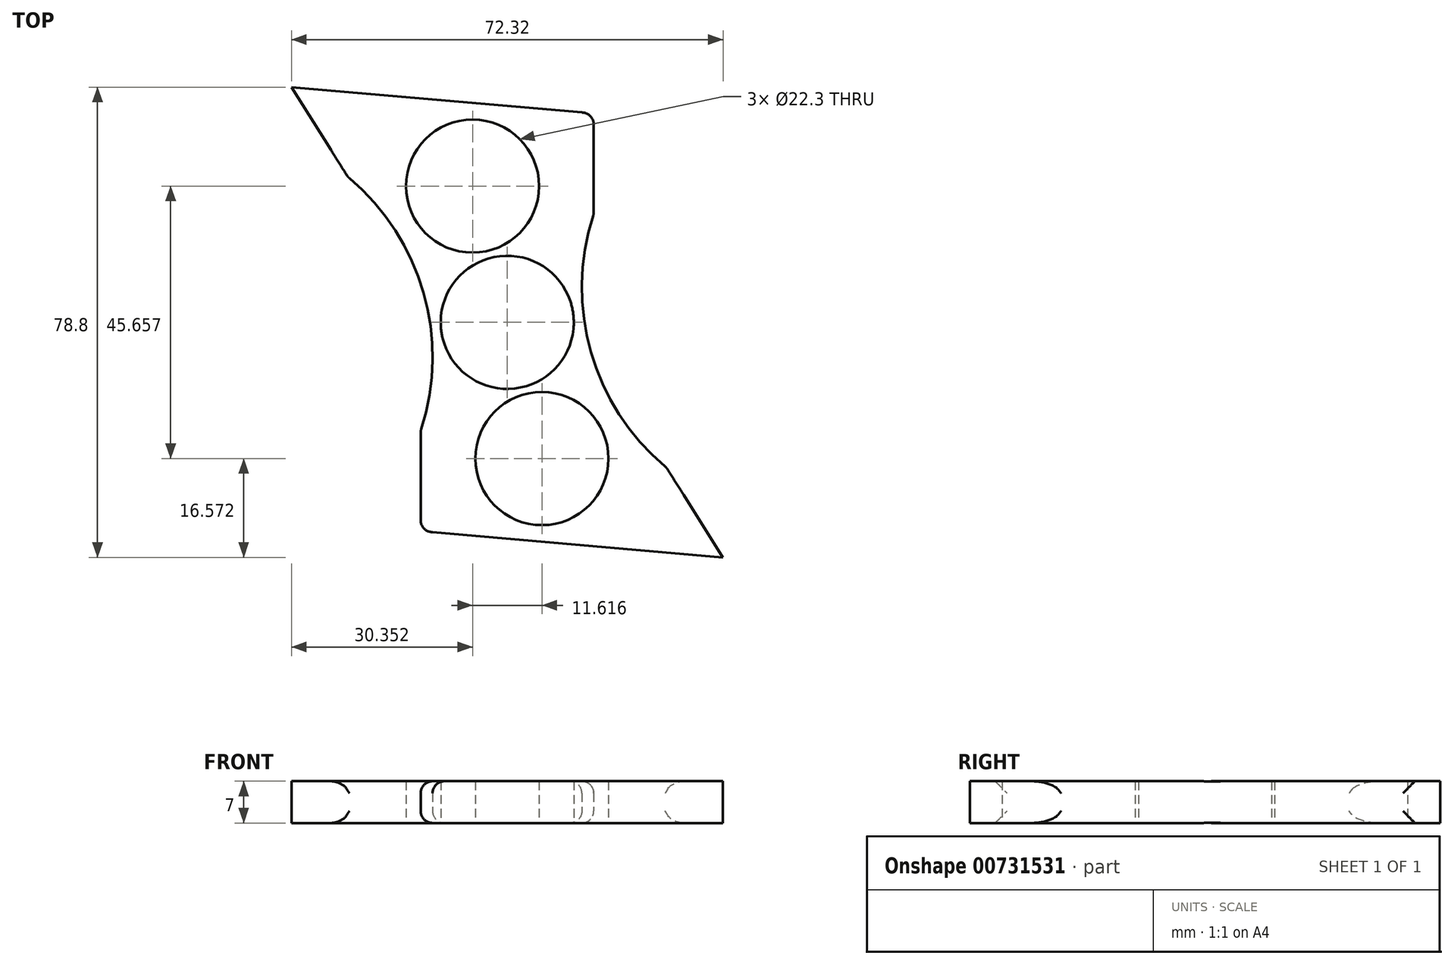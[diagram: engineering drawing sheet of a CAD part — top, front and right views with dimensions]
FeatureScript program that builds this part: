
annotation { "Feature Type Name" : "Feature", "Feature Type Description" : "" }
export const myFeature = defineFeature(function(context is Context, id is Id, definition is map)
    precondition{}
    {
        {
            var Q0;
            Q0=qCreatedBy(makeId("Top.planeOp"),FACE);
            var sketch = newSketch(context, id + "F0", { "sketchPlane" : qUnion([Q0])});
            skCircle(sketch, "E0", {"center": v(0, 0) * mm, "radius": 11.15 * mm});
            skArc(sketch, "E1", {"start": v(-12.54, -7.28) * mm, "mid": v(1.63, -14.4) * mm, "end": v(13.85, -4.3) * mm});
            skLineSegment(sketch, "E2", {"start": v(-14.5, -18.17) * mm, "end": v(-14.5, -40) * mm});
            skCircle(sketch, "E3", {"center": v(-5.8, 22.83) * mm, "radius": 11.15 * mm});
            skLineSegment(sketch, "E4", {"start": v(-26.68, 24.35) * mm, "end": v(-36.16, 39.4) * mm});
            skLineSegment(sketch, "E5", {"start": v(14.5, 18.17) * mm, "end": v(14.5, 35) * mm});
            skLineSegment(sketch, "E6", {"start": v(14.5, 35) * mm, "end": v(-36.16, 39.4) * mm});
            skLineSegment(sketch, "E7.1.0", {"start": v(-14.5, -35) * mm, "end": v(36.16, -39.4) * mm});
            skLineSegment(sketch, "E7.1.1", {"start": v(26.68, -24.35) * mm, "end": v(36.16, -39.4) * mm});
            skCircle(sketch, "E7.1.2", {"center": v(5.8, -22.83) * mm, "radius": 11.15 * mm});
            skArc(sketch, "E8", {"start": v(-14.5, -18.17) * mm, "mid": v(-14.03, 4.97) * mm, "end": v(-26.68, 24.35) * mm});
            skPoint(sketch, "E9.orphan", {"position": v(-14.5, 0) * mm});
            skArc(sketch, "E10.1.0", {"start": v(14.5, 18.17) * mm, "mid": v(14.03, -4.97) * mm, "end": v(26.68, -24.35) * mm});
            skPoint(sketch, "E11.orphan", {"position": v(14.5, 0) * mm});
            skArc(sketch, "E12.trimOffspring", {"start": v(12.54, 7.28) * mm, "mid": v(-1.63, 14.4) * mm, "end": v(-13.85, 4.3) * mm});
            skPoint(sketch, "E13.orphan", {"position": v(14.5, -5) * mm});
            skSolve(sketch);
        }
        {
            var Q0;
            {var subQ0=sQuery(id+"F0.wireOp",EDGE,"iOKIUNUS-VdLY-p6A8-uHDL-GzDrufJryVfl");Q0=makeQuery(id+"F0.imprint","IMPRINT",FACE,{"disambiguationData":[TD([[makeQuery(id+"F0.imprint","IMPRINT",EDGE,{"derivedFrom":subQ0}),-1.0]])]});}
            var Q1;
            Q1=makeQuery(id+"F0.imprint","IMPRINT",FACE,{"disambiguationData":[TD([[makeQuery(id+"F0.imprint","IMPRINT",EDGE,{"derivedFrom":sQuery(id+"F0.wireOp",EDGE,"E0")}),-1.0]])]});
            var Q2;
            {var subQ0=sQuery(id+"F0.wireOp",EDGE,"E7.1.0");Q2=makeQuery(id+"F0.imprint","IMPRINT",FACE,{"disambiguationData":[TD([[makeQuery(id+"F0.imprint","IMPRINT",EDGE,{"derivedFrom":subQ0}),1.0]])]});}
            var Q3;
            {var subQ6=sQuery(id+"F0.wireOp",EDGE,"E4");Q3=makeQuery(id+"F0.imprint","IMPRINT",FACE,{"disambiguationData":[TD([[makeQuery(id+"F0.imprint","IMPRINT",EDGE,{"derivedFrom":subQ6}),-1.0]])]});}
            extrude(context, id + "F1", {"entities" : qUnion([Q0, Q1, Q2, Q3]), "depth" : 7 * mm, "offsetDistance" : 25 * mm});
        }
        {
            var Q0;
            Q0=makeQuery(id+"F1.opExtrude","SWEPT_FACE",FACE,{"disambiguationData":[OSD([sQuery(id+"F0.wireOp",EDGE,"E8")])]});
            var Q1;
            Q1=makeQuery(id+"F1.opExtrude","SWEPT_FACE",FACE,{"disambiguationData":[OSD([sQuery(id+"F0.wireOp",EDGE,"E10.1.0")])]});
            var Q2;
            Q2=makeQuery(id+"F1.opExtrude","SWEPT_FACE",FACE,{"disambiguationData":[OSD([sQuery(id+"F0.wireOp",EDGE,"E2")])]});
            var Q3;
            Q3=makeQuery(id+"F1.opExtrude","SWEPT_FACE",FACE,{"disambiguationData":[OSD([sQuery(id+"F0.wireOp",EDGE,"E5")])]});
            fillet(context, id + "F2", {"entities" : qUnion([Q0, Q1, Q2, Q3]), "radius" : 2 * mm, "tangentPropagation" : true, "allowEdgeOverflow" : false});
        }
    });
